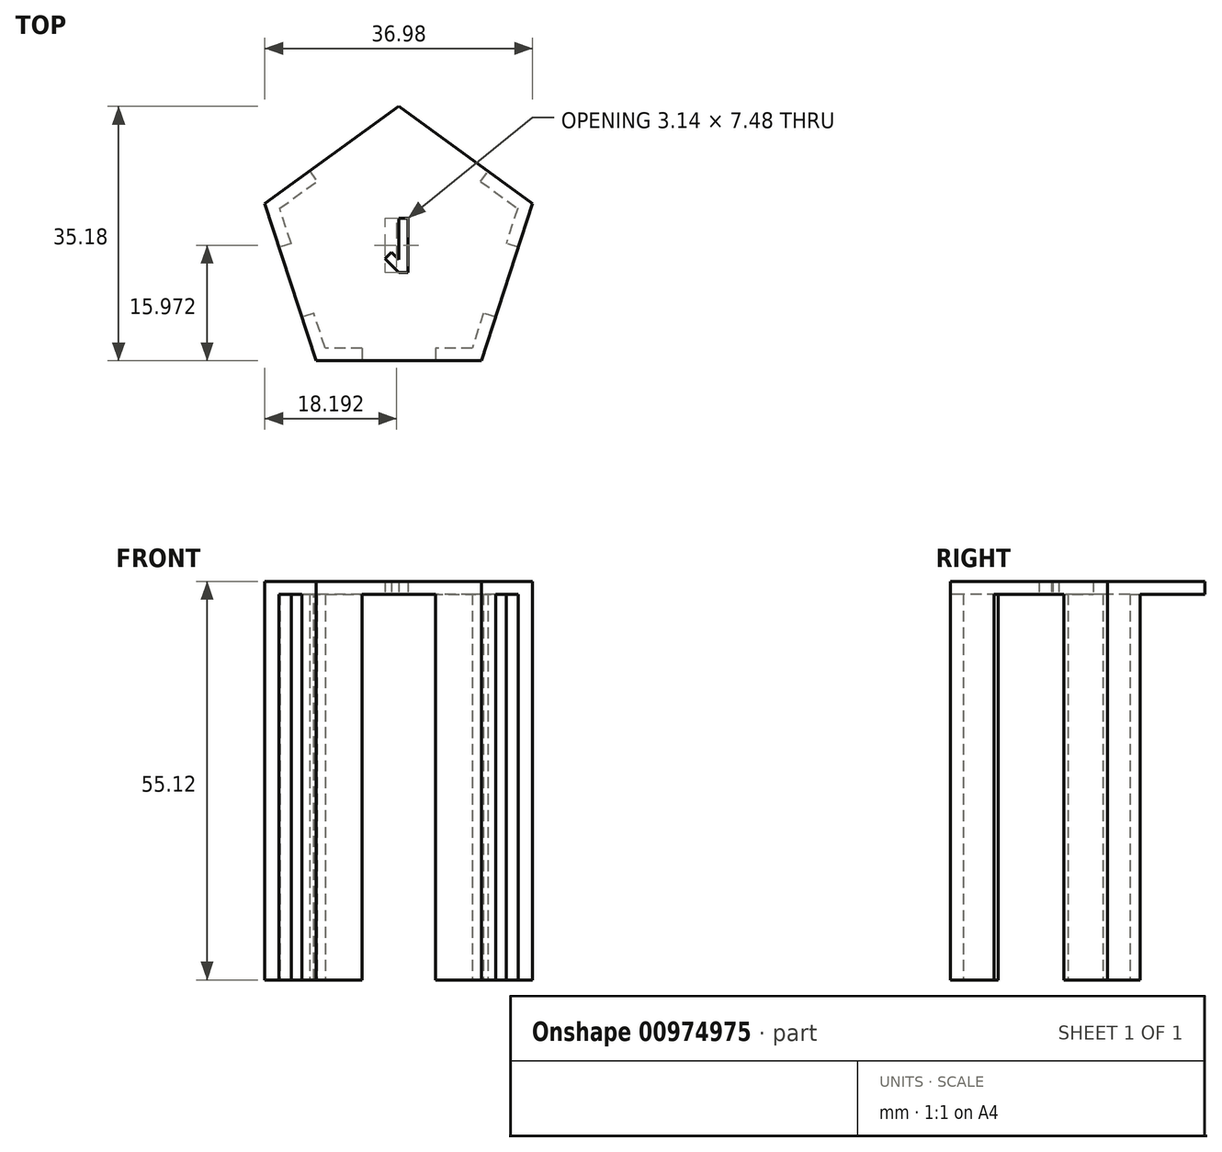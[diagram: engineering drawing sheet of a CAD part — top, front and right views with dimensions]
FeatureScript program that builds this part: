
annotation { "Feature Type Name" : "Feature", "Feature Type Description" : "" }
export const myFeature = defineFeature(function(context is Context, id is Id, definition is map)
    precondition{}
    {
        {
            var Q0;
            Q0=qCreatedBy(makeId("Top.planeOp"),FACE);
            var sketch = newSketch(context, id + "F0", { "sketchPlane" : qUnion([Q0])});
            skCircle(sketch, "E0.cCircle", {"center": v(0, 0) * mm, "radius": 19.45 * mm, "construction": true});
            skLineSegment(sketch, "E0.0", {"start": v(11.43, -15.73) * mm, "end": v(-11.43, -15.73) * mm});
            skLineSegment(sketch, "E0.1", {"start": v(-11.43, -15.73) * mm, "end": v(-18.5, 6) * mm});
            skLineSegment(sketch, "E0.2", {"start": v(-18.5, 6) * mm, "end": v(0, 19.45) * mm});
            skLineSegment(sketch, "E0.3", {"start": v(0, 19.45) * mm, "end": v(18.5, 6) * mm});
            skLineSegment(sketch, "E0.4", {"start": v(18.5, 6) * mm, "end": v(11.43, -15.73) * mm});
            skSolve(sketch);
        }
        {
            var Q0;
            Q0=makeQuery(id+"F0.imprint","IMPRINT",FACE,{"disambiguationData":[TD([[makeQuery(id+"F0.imprint","IMPRINT",EDGE,{"derivedFrom":sQuery(id+"F0.wireOp",EDGE,"E0.0")}),-1.0]])]});
            extrude(context, id + "F1", {"entities" : qUnion([Q0]), "depth" : 55.12 * mm, "offsetDistance" : 25.4 * mm});
        }
        {
            var Q0;
            Q0=qCreatedBy(makeId("Top.planeOp"),FACE);
            var sketch = newSketch(context, id + "F2", { "sketchPlane" : qUnion([Q0])});
            skCircle(sketch, "E1.cCircle", {"center": v(0, 0) * mm, "radius": 13.98 * mm, "construction": true});
            skLineSegment(sketch, "E1.0", {"start": v(16.44, 5.34) * mm, "end": v(10.16, -13.98) * mm});
            skLineSegment(sketch, "E1.1", {"start": v(10.16, -13.98) * mm, "end": v(-10.16, -13.98) * mm});
            skLineSegment(sketch, "E1.2", {"start": v(-10.16, -13.98) * mm, "end": v(-16.44, 5.34) * mm});
            skLineSegment(sketch, "E1.3", {"start": v(-16.44, 5.34) * mm, "end": v(0, 17.29) * mm});
            skLineSegment(sketch, "E1.4", {"start": v(0, 17.29) * mm, "end": v(16.44, 5.34) * mm});
            skPoint(sketch, "E1.0.midPoint", {"position": v(13.3, -4.32) * mm});
            skSolve(sketch);
        }
        {
            var Q0;
            Q0=qSketchRegion(id+"F2",true);
            extrude(context, id + "F3", {"entities" : qUnion([Q0]), "operationType" : NewBodyOperationType.REMOVE, "depth" : 53.34 * mm, "offsetDistance" : 25.4 * mm});
        }
        {
            var Q0;
            Q0=makeQuery(id+"F1.opExtrude","CAP_FACE",FACE,{"disambiguationData":[OSD([sQuery(id+"F0.wireOp",EDGE,"E0.0"),sQuery(id+"F0.wireOp",EDGE,"E0.1"),sQuery(id+"F0.wireOp",EDGE,"E0.2"),sQuery(id+"F0.wireOp",EDGE,"E0.3"),sQuery(id+"F0.wireOp",EDGE,"E0.4")])],"isStart":true});
            var sketch = newSketch(context, id + "F4", { "sketchPlane" : qUnion([Q0])});
            skLineSegment(sketch, "E2", {"start": v(0, 0) * mm, "end": v(23.62, 7.67) * mm});
            skLineSegment(sketch, "E3", {"start": v(0, 0) * mm, "end": v(-35.57, 11.56) * mm});
            skLineSegment(sketch, "E4", {"start": v(0, 0) * mm, "end": v(0, -28.1) * mm});
            skLineSegment(sketch, "E5.bottom", {"start": v(-11.25, -1.69) * mm, "end": v(-18.5, 0.67) * mm});
            skLineSegment(sketch, "E5.top", {"start": v(-8.1, 7.98) * mm, "end": v(-15.35, 10.33) * mm});
            skLineSegment(sketch, "E5.left", {"start": v(-11.25, -1.69) * mm, "end": v(-8.1, 7.98) * mm});
            skLineSegment(sketch, "E5.right", {"start": v(-18.5, 0.67) * mm, "end": v(-15.35, 10.33) * mm});
            skPoint(sketch, "E5.middle", {"position": v(-13.3, 4.32) * mm});
            skLineSegment(sketch, "E6.bottom", {"start": v(18.5, 0.67) * mm, "end": v(11.25, -1.69) * mm});
            skLineSegment(sketch, "E6.top", {"start": v(15.35, 10.33) * mm, "end": v(8.1, 7.98) * mm});
            skLineSegment(sketch, "E6.left", {"start": v(18.5, 0.67) * mm, "end": v(15.35, 10.33) * mm});
            skLineSegment(sketch, "E6.right", {"start": v(11.25, -1.69) * mm, "end": v(8.1, 7.98) * mm});
            skPoint(sketch, "E6.middle", {"position": v(13.3, 4.32) * mm});
            skLineSegment(sketch, "E7.bottom", {"start": v(5.08, 10.17) * mm, "end": v(-5.08, 10.17) * mm});
            skLineSegment(sketch, "E7.top", {"start": v(5.08, 17.8) * mm, "end": v(-5.08, 17.8) * mm});
            skLineSegment(sketch, "E7.left", {"start": v(5.08, 10.17) * mm, "end": v(5.08, 17.8) * mm});
            skLineSegment(sketch, "E7.right", {"start": v(-5.08, 10.17) * mm, "end": v(-5.08, 17.8) * mm});
            skPoint(sketch, "E7.middle", {"position": v(0, 13.98) * mm});
            skLineSegment(sketch, "E8", {"start": v(-12.33, -10.49) * mm, "end": v(-11.3, -9.07) * mm});
            skLineSegment(sketch, "E9", {"start": v(11.3, -9.07) * mm, "end": v(12.33, -10.49) * mm});
            skLineSegment(sketch, "E10", {"start": v(-11.3, -9.07) * mm, "end": v(11.3, -9.07) * mm});
            skLineSegment(sketch, "E11", {"start": v(-12.33, -10.49) * mm, "end": v(0, -28.1) * mm});
            skLineSegment(sketch, "E12", {"start": v(12.33, -10.49) * mm, "end": v(0, -28.1) * mm});
            skSolve(sketch);
        }
        {
            var Q0;
            {var subQ0=sQuery(id+"F4.wireOp",EDGE,"E3");var subQ1=makeQuery(id+"F3.boolean.opBoolean","COPY",EDGE,{"derivedFrom":makeQuery(id+"F3.opExtrude","CAP_EDGE",EDGE,{"disambiguationData":[OSD([sQuery(id+"F2.wireOp",EDGE,"E1.2")])],"isStart":true})});var subQ2=makeQuery(id+"F4.imprint","INTERSECT",VERTEX,{"derivedFrom":[subQ1,subQ0]});Q0=makeQuery(id+"F4.imprint","IMPRINT",FACE,{"disambiguationData":[TD([[makeQuery(id+"F4.imprint","IMPRINT",EDGE,{"disambiguationData":[TD([[subQ2,-1.0]])],"derivedFrom":subQ0}),1.0]])]});}
            var Q1;
            {var subQ0=sQuery(id+"F4.wireOp",EDGE,"E3");var subQ1=makeQuery(id+"F3.boolean.opBoolean","COPY",EDGE,{"derivedFrom":makeQuery(id+"F3.opExtrude","CAP_EDGE",EDGE,{"disambiguationData":[OSD([sQuery(id+"F2.wireOp",EDGE,"E1.2")])],"isStart":true})});var subQ2=makeQuery(id+"F4.imprint","INTERSECT",VERTEX,{"derivedFrom":[subQ1,subQ0]});Q1=makeQuery(id+"F4.imprint","IMPRINT",FACE,{"disambiguationData":[TD([[makeQuery(id+"F4.imprint","IMPRINT",EDGE,{"disambiguationData":[TD([[subQ2,-1.0]])],"derivedFrom":subQ0}),-1.0]])]});}
            var Q2;
            {var subQ0=sQuery(id+"F4.wireOp",EDGE,"E2");var subQ1=makeQuery(id+"F3.boolean.opBoolean","COPY",EDGE,{"derivedFrom":makeQuery(id+"F3.opExtrude","CAP_EDGE",EDGE,{"disambiguationData":[OSD([sQuery(id+"F2.wireOp",EDGE,"E1.0")])],"isStart":true})});var subQ2=makeQuery(id+"F4.imprint","INTERSECT",VERTEX,{"derivedFrom":[subQ1,subQ0]});Q2=makeQuery(id+"F4.imprint","IMPRINT",FACE,{"disambiguationData":[TD([[makeQuery(id+"F4.imprint","IMPRINT",EDGE,{"disambiguationData":[TD([[subQ2,-1.0]])],"derivedFrom":subQ0}),1.0]])]});}
            var Q3;
            {var subQ0=sQuery(id+"F4.wireOp",EDGE,"E2");var subQ1=makeQuery(id+"F3.boolean.opBoolean","COPY",EDGE,{"derivedFrom":makeQuery(id+"F3.opExtrude","CAP_EDGE",EDGE,{"disambiguationData":[OSD([sQuery(id+"F2.wireOp",EDGE,"E1.0")])],"isStart":true})});var subQ2=makeQuery(id+"F4.imprint","INTERSECT",VERTEX,{"derivedFrom":[subQ1,subQ0]});Q3=makeQuery(id+"F4.imprint","IMPRINT",FACE,{"disambiguationData":[TD([[makeQuery(id+"F4.imprint","IMPRINT",EDGE,{"disambiguationData":[TD([[subQ2,-1.0]])],"derivedFrom":subQ0}),-1.0]])]});}
            var Q4;
            {var subQ1=makeQuery(id+"F1.opExtrude","CAP_EDGE",EDGE,{"disambiguationData":[OSD([sQuery(id+"F0.wireOp",EDGE,"E0.2")])],"isStart":true});var subQ5=sQuery(id+"F4.wireOp",EDGE,"VIOiiu8y-qDuE-E9mX-nsSh-dz9hzi8E33ez.right");var subQ6=makeQuery(id+"F4.imprint","INTERSECT",VERTEX,{"derivedFrom":[subQ1,subQ5]});Q4=makeQuery(id+"F4.imprint","IMPRINT",FACE,{"disambiguationData":[TD([[makeQuery(id+"F4.imprint","IMPRINT",EDGE,{"disambiguationData":[TD([[subQ6,-1.0]])],"derivedFrom":subQ5}),-1.0]])]});}
            var Q5;
            {var subQ1=makeQuery(id+"F1.opExtrude","CAP_EDGE",EDGE,{"disambiguationData":[OSD([sQuery(id+"F0.wireOp",EDGE,"E0.3")])],"isStart":true});var subQ5=sQuery(id+"F4.wireOp",EDGE,"VIOiiu8y-qDuE-E9mX-nsSh-dz9hzi8E33ez.left");var subQ6=makeQuery(id+"F4.imprint","INTERSECT",VERTEX,{"derivedFrom":[subQ1,subQ5]});Q5=makeQuery(id+"F4.imprint","IMPRINT",FACE,{"disambiguationData":[TD([[makeQuery(id+"F4.imprint","IMPRINT",EDGE,{"disambiguationData":[TD([[subQ6,-1.0]])],"derivedFrom":subQ5}),1.0]])]});}
            var Q6;
            {var subQ0=sQuery(id+"F4.wireOp",EDGE,"E7.left");var subQ1=makeQuery(id+"F1.opExtrude","CAP_EDGE",EDGE,{"disambiguationData":[OSD([sQuery(id+"F0.wireOp",EDGE,"E0.0")])],"isStart":true});var subQ2=makeQuery(id+"F4.imprint","INTERSECT",VERTEX,{"derivedFrom":[subQ1,subQ0]});Q6=makeQuery(id+"F4.imprint","IMPRINT",FACE,{"disambiguationData":[TD([[makeQuery(id+"F4.imprint","IMPRINT",EDGE,{"disambiguationData":[TD([[subQ2,1.0]])],"derivedFrom":subQ0}),1.0]])]});}
            var Q7;
            {var subQ5=sQuery(id+"F4.wireOp",EDGE,"E8");Q7=makeQuery(id+"F4.imprint","IMPRINT",FACE,{"disambiguationData":[TD([[makeQuery(id+"F4.imprint","IMPRINT",EDGE,{"derivedFrom":subQ5}),-1.0]])]});}
            var Q8;
            {var subQ5=sQuery(id+"F4.wireOp",EDGE,"E9");Q8=makeQuery(id+"F4.imprint","IMPRINT",FACE,{"disambiguationData":[TD([[makeQuery(id+"F4.imprint","IMPRINT",EDGE,{"derivedFrom":subQ5}),-1.0]])]});}
            extrude(context, id + "F5", {"entities" : qUnion([Q0, Q1, Q2, Q3, Q4, Q5, Q6, Q7, Q8]), "operationType" : NewBodyOperationType.REMOVE, "oppositeDirection" : true, "depth" : 53.34 * mm, "offsetDistance" : 25.4 * mm});
        }
        {
            var Q0;
            {var subQ0=sQuery(id+"F2.wireOp",EDGE,"E1.4");var subQ1=sQuery(id+"F2.wireOp",EDGE,"E1.3");var subQ2=sQuery(id+"F2.wireOp",EDGE,"E1.1");var subQ3=sQuery(id+"F2.wireOp",EDGE,"E1.0");var subQ4=sQuery(id+"F2.wireOp",EDGE,"E1.2");Q0=makeQuery(id+"F5.boolean.opBoolean","MERGE",FACE,{"derivedFrom":[makeQuery(id+"F3.boolean.opBoolean","COPY",FACE,{"derivedFrom":makeQuery(id+"F3.opExtrude","CAP_FACE",FACE,{"disambiguationData":[OSD([subQ3,subQ2,subQ4,subQ1,subQ0])],"isStart":false})})],"fromTools":[makeQuery(id+"F5.opExtrude","CAP_FACE",FACE,{"disambiguationData":[OSD([sQuery(id+"F0.wireOp",EDGE,"E0.1"),subQ4,sQuery(id+"F4.wireOp",EDGE,"E5.bottom"),sQuery(id+"F4.wireOp",EDGE,"E5.top")])],"isStart":false}),makeQuery(id+"F5.opExtrude","CAP_FACE",FACE,{"disambiguationData":[OSD([sQuery(id+"F0.wireOp",EDGE,"E0.4"),subQ3,sQuery(id+"F4.wireOp",EDGE,"E6.bottom"),sQuery(id+"F4.wireOp",EDGE,"E6.top")])],"isStart":false}),makeQuery(id+"F5.opExtrude","CAP_FACE",FACE,{"disambiguationData":[OSD([sQuery(id+"F0.wireOp",EDGE,"E0.0"),subQ2,sQuery(id+"F4.wireOp",EDGE,"E7.left"),sQuery(id+"F4.wireOp",EDGE,"E7.right")])],"isStart":false}),makeQuery(id+"F5.opExtrude","CAP_FACE",FACE,{"disambiguationData":[OSD([sQuery(id+"F0.wireOp",EDGE,"E0.2"),sQuery(id+"F0.wireOp",EDGE,"E0.3"),subQ1,subQ0,sQuery(id+"F4.wireOp",EDGE,"E8"),sQuery(id+"F4.wireOp",EDGE,"E9")])],"isStart":false})]});}
            var sketch = newSketch(context, id + "F6", { "sketchPlane" : qUnion([Q0])});
            skText(sketch, "E13", { "text": "1", "fontName": "AllertaStencil-Regular.ttf"});
            const initialGuessF6  = {"E13": [-0.00216, -0.00398, 1, 0, 0.00748]};
            skSetInitialGuess(sketch, initialGuessF6);
            skSolve(sketch);
        }
        {
            var Q0;
            Q0=makeQuery(id+"F6.imprint","IMPRINT",FACE,{"disambiguationData":[TD([[makeQuery(id+"F6.imprint","IMPRINT",EDGE,{"derivedFrom":sQuery(id+"F6.wireOp",EDGE,"E13.sketch_text.stroke-0")}),-1.0]])]});
            extrude(context, id + "F7", {"entities" : qUnion([Q0]), "operationType" : NewBodyOperationType.REMOVE, "oppositeDirection" : true, "depth" : 25.4 * mm, "offsetDistance" : 25.4 * mm});
        }
    });
